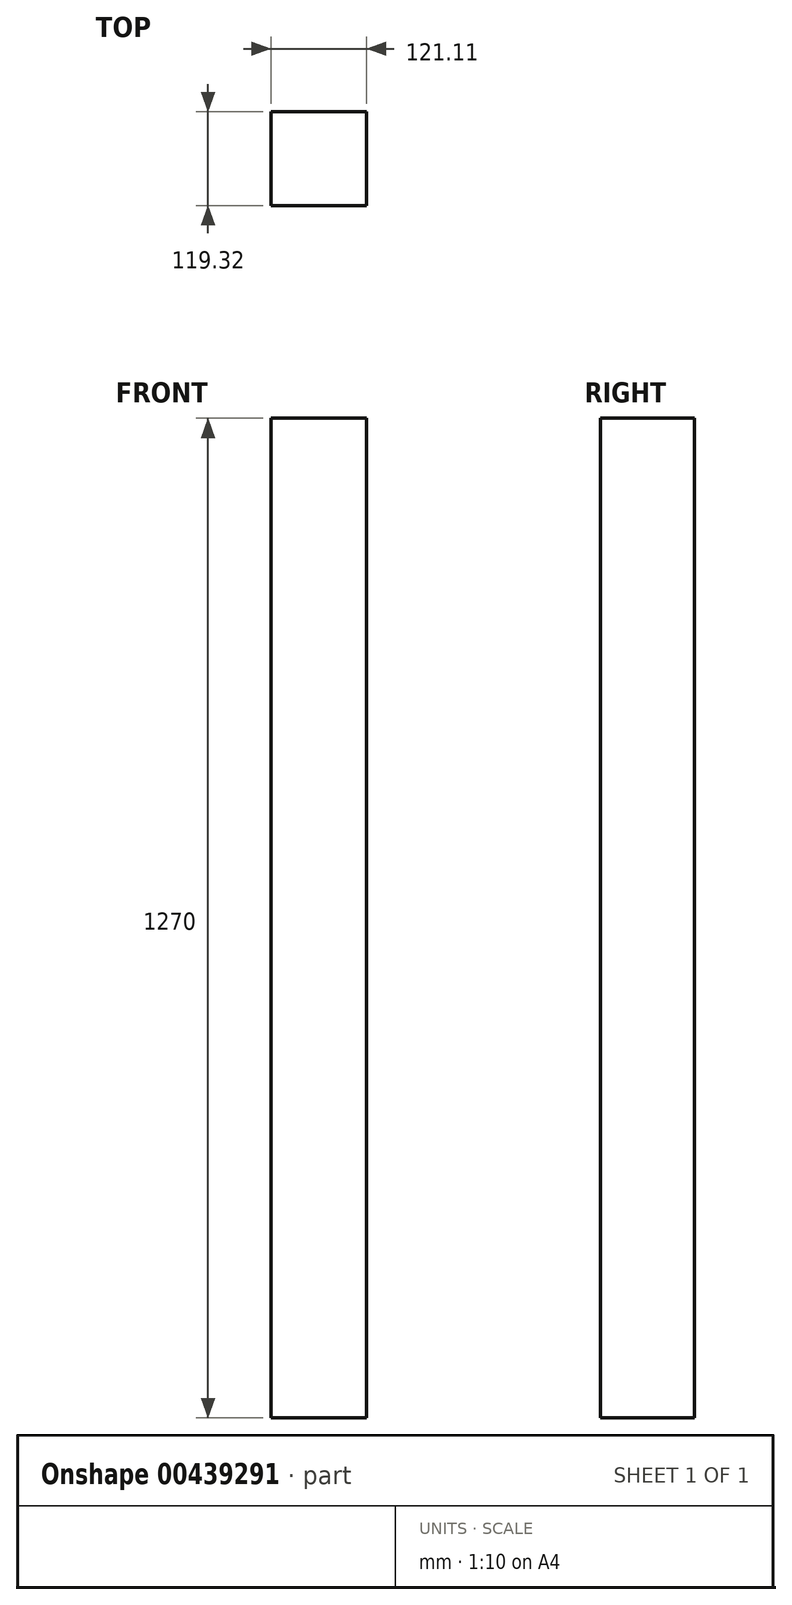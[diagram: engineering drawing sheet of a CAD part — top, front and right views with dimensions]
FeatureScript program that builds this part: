
annotation { "Feature Type Name" : "Feature", "Feature Type Description" : "" }
export const myFeature = defineFeature(function(context is Context, id is Id, definition is map)
    precondition{}
    {
        {
            var Q0;
            Q0=qCreatedBy(makeId("Top.planeOp"),FACE);
            var sketch = newSketch(context, id + "F0", { "sketchPlane" : qUnion([Q0])});
            skLineSegment(sketch, "E0.bottom", {"start": v(75.15, -72.6) * mm, "end": v(-45.96, -72.6) * mm});
            skLineSegment(sketch, "E0.top", {"start": v(75.15, 46.72) * mm, "end": v(-45.96, 46.72) * mm});
            skLineSegment(sketch, "E0.left", {"start": v(75.15, -72.6) * mm, "end": v(75.15, 46.72) * mm});
            skLineSegment(sketch, "E0.right", {"start": v(-45.96, -72.6) * mm, "end": v(-45.96, 46.72) * mm});
            skSolve(sketch);
        }
        {
            var Q0;
            Q0=makeQuery(id+"F0.imprint","IMPRINT",FACE,{"disambiguationData":[TD([[makeQuery(id+"F0.imprint","IMPRINT",EDGE,{"derivedFrom":sQuery(id+"F0.wireOp",EDGE,"E0.bottom")}),-1.0]])]});
            extrude(context, id + "F1", {"entities" : qUnion([Q0]), "depth" : 1270 * mm});
        }
    });
